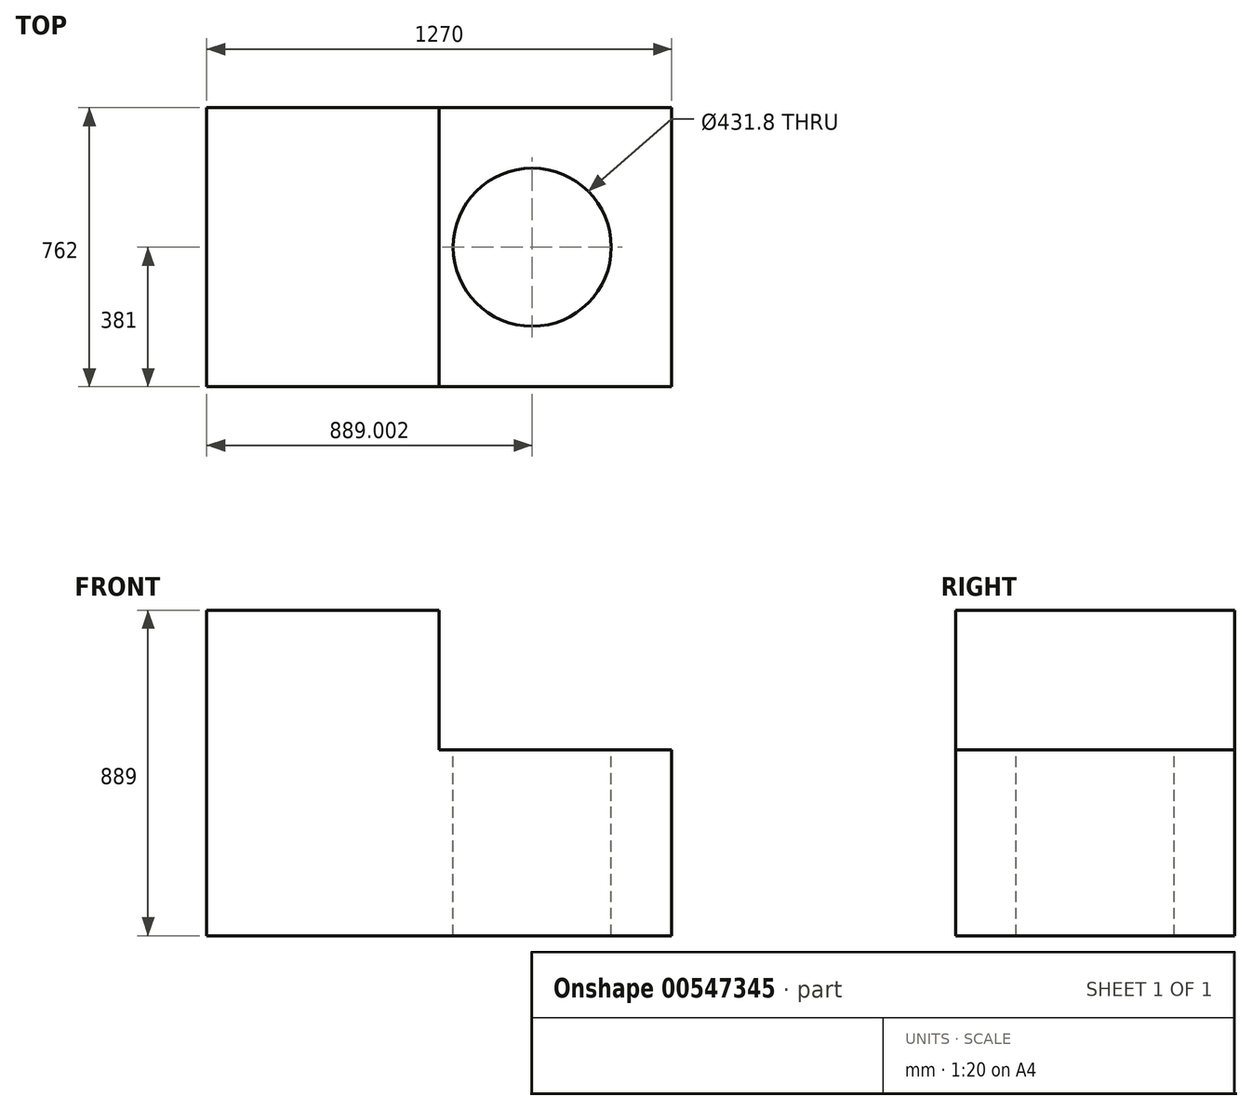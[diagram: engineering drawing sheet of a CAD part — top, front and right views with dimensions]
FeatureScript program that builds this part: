
annotation { "Feature Type Name" : "Feature", "Feature Type Description" : "" }
export const myFeature = defineFeature(function(context is Context, id is Id, definition is map)
    precondition{}
    {
        {
            var Q0;
            Q0=qCreatedBy(makeId("Front.planeOp"),FACE);
            var sketch = newSketch(context, id + "F0", { "sketchPlane" : qUnion([Q0])});
            skLineSegment(sketch, "E0.bottom", {"start": v(-604.92, 381) * mm, "end": v(30.08, 381) * mm});
            skLineSegment(sketch, "E0.top", {"start": v(-604.92, -508) * mm, "end": v(665.08, -508) * mm});
            skLineSegment(sketch, "E0.left", {"start": v(-604.92, 381) * mm, "end": v(-604.92, -508) * mm});
            skLineSegment(sketch, "E0.right", {"start": v(665.08, 0) * mm, "end": v(665.08, -508) * mm});
            skLineSegment(sketch, "E1", {"start": v(30.08, 381) * mm, "end": v(30.08, 0) * mm});
            skLineSegment(sketch, "E2", {"start": v(30.08, 0) * mm, "end": v(665.08, 0) * mm});
            skSolve(sketch);
        }
        {
            var Q0;
            Q0=qSketchRegion(id+"F0",true);
            extrude(context, id + "F1", {"entities" : qUnion([Q0]), "depth" : 762 * mm, "offsetDistance" : 25.4 * mm});
        }
        {
            var Q0;
            Q0=makeQuery(id+"F1.opExtrude","SWEPT_FACE",FACE,{"disambiguationData":[OSD([sQuery(id+"F0.wireOp",EDGE,"E2")])]});
            var sketch = newSketch(context, id + "F2", { "sketchPlane" : qUnion([Q0])});
            skCircle(sketch, "E3", {"center": v(284.08, -381) * mm, "radius": 215.9 * mm});
            skSolve(sketch);
        }
        {
            var Q0;
            Q0=qSketchRegion(id+"F2",true);
            extrude(context, id + "F3", {"entities" : qUnion([Q0]), "operationType" : NewBodyOperationType.REMOVE, "oppositeDirection" : true, "depth" : 508 * mm, "offsetDistance" : 25.4 * mm});
        }
    });
